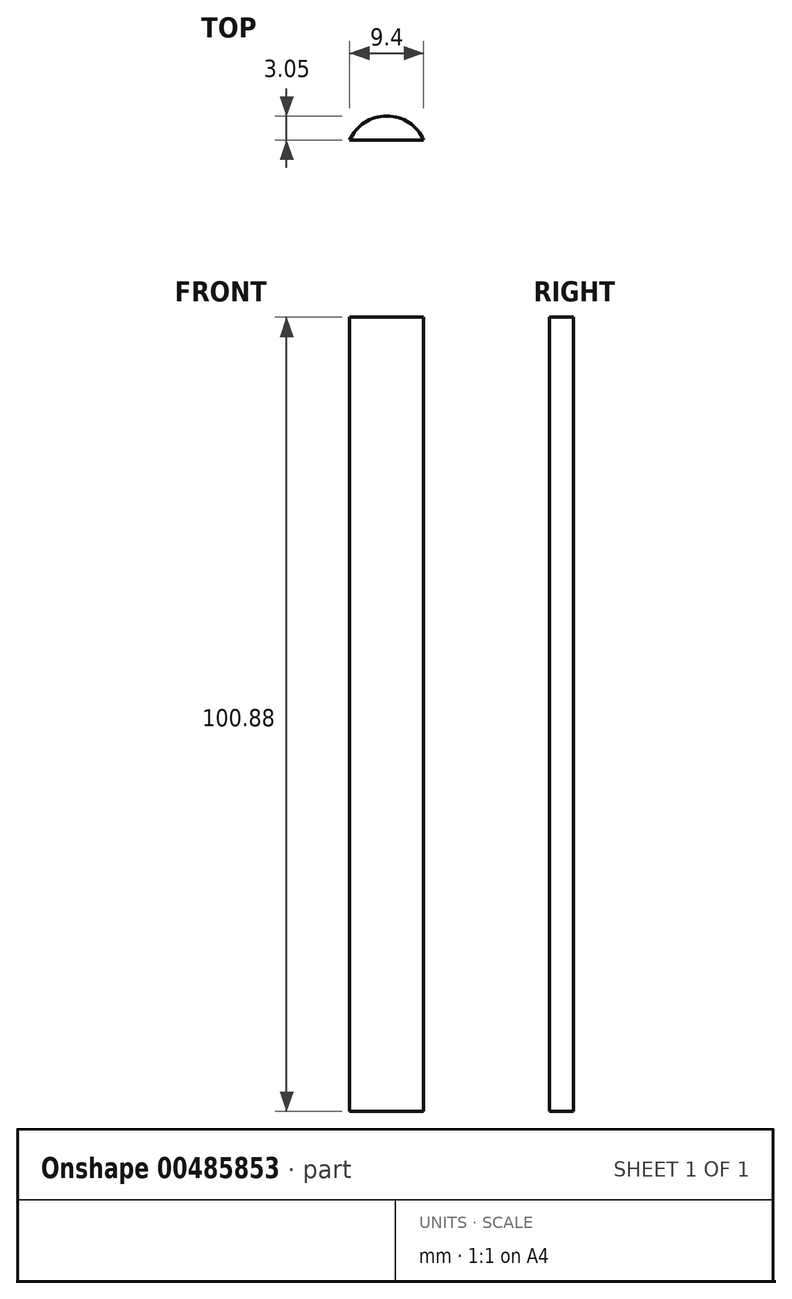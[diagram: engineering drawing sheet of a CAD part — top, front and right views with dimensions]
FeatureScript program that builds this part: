
annotation { "Feature Type Name" : "Feature", "Feature Type Description" : "" }
export const myFeature = defineFeature(function(context is Context, id is Id, definition is map)
    precondition{}
    {
        {
            var Q0;
            Q0=qCreatedBy(makeId("Front.planeOp"),FACE);
            var sketch = newSketch(context, id + "F0", { "sketchPlane" : qUnion([Q0])});
            skLineSegment(sketch, "E0.bottom", {"start": v(-15.42, 39.04) * mm, "end": v(-6.02, 39.04) * mm});
            skLineSegment(sketch, "E0.top", {"start": v(-15.42, -45.07) * mm, "end": v(-6.02, -45.07) * mm});
            skLineSegment(sketch, "E0.left", {"start": v(-15.42, 39.04) * mm, "end": v(-15.42, -45.07) * mm});
            skLineSegment(sketch, "E0.right", {"start": v(-6.02, 39.04) * mm, "end": v(-6.02, -45.07) * mm});
            skSolve(sketch);
        }
        {
            var Q0;
            Q0=makeQuery(id+"F0.imprint","IMPRINT",FACE,{"disambiguationData":[TD([[makeQuery(id+"F0.imprint","IMPRINT",EDGE,{"derivedFrom":sQuery(id+"F0.wireOp",EDGE,"E0.bottom")}),-1.0]])]});
            extrude(context, id + "F1", {"entities" : qUnion([Q0]), "depth" : 3.05 * mm});
        }
        {
            var Q0;
            Q0=makeQuery(id+"F1.opExtrude","CAP_EDGE",EDGE,{"disambiguationData":[OSD([sQuery(id+"F0.wireOp",EDGE,"E0.right")])],"isStart":true});
            var Q1;
            Q1=makeQuery(id+"F1.opExtrude","CAP_EDGE",EDGE,{"disambiguationData":[OSD([sQuery(id+"F0.wireOp",EDGE,"E0.left")])],"isStart":true});
            fillet(context, id + "F2", {"entities" : qUnion([Q0, Q1]), "radius" : 5.08 * mm, "tangentPropagation" : true, "allowEdgeOverflow" : false});
        }
        {
            var Q0;
            Q0=makeQuery(id+"F1.opExtrude","SWEPT_FACE",FACE,{"disambiguationData":[OSD([sQuery(id+"F0.wireOp",EDGE,"E0.bottom")])]});
            extrude(context, id + "F3", {"entities" : qUnion([Q0]), "operationType" : NewBodyOperationType.ADD, "depth" : 16.76 * mm});
        }
    });
